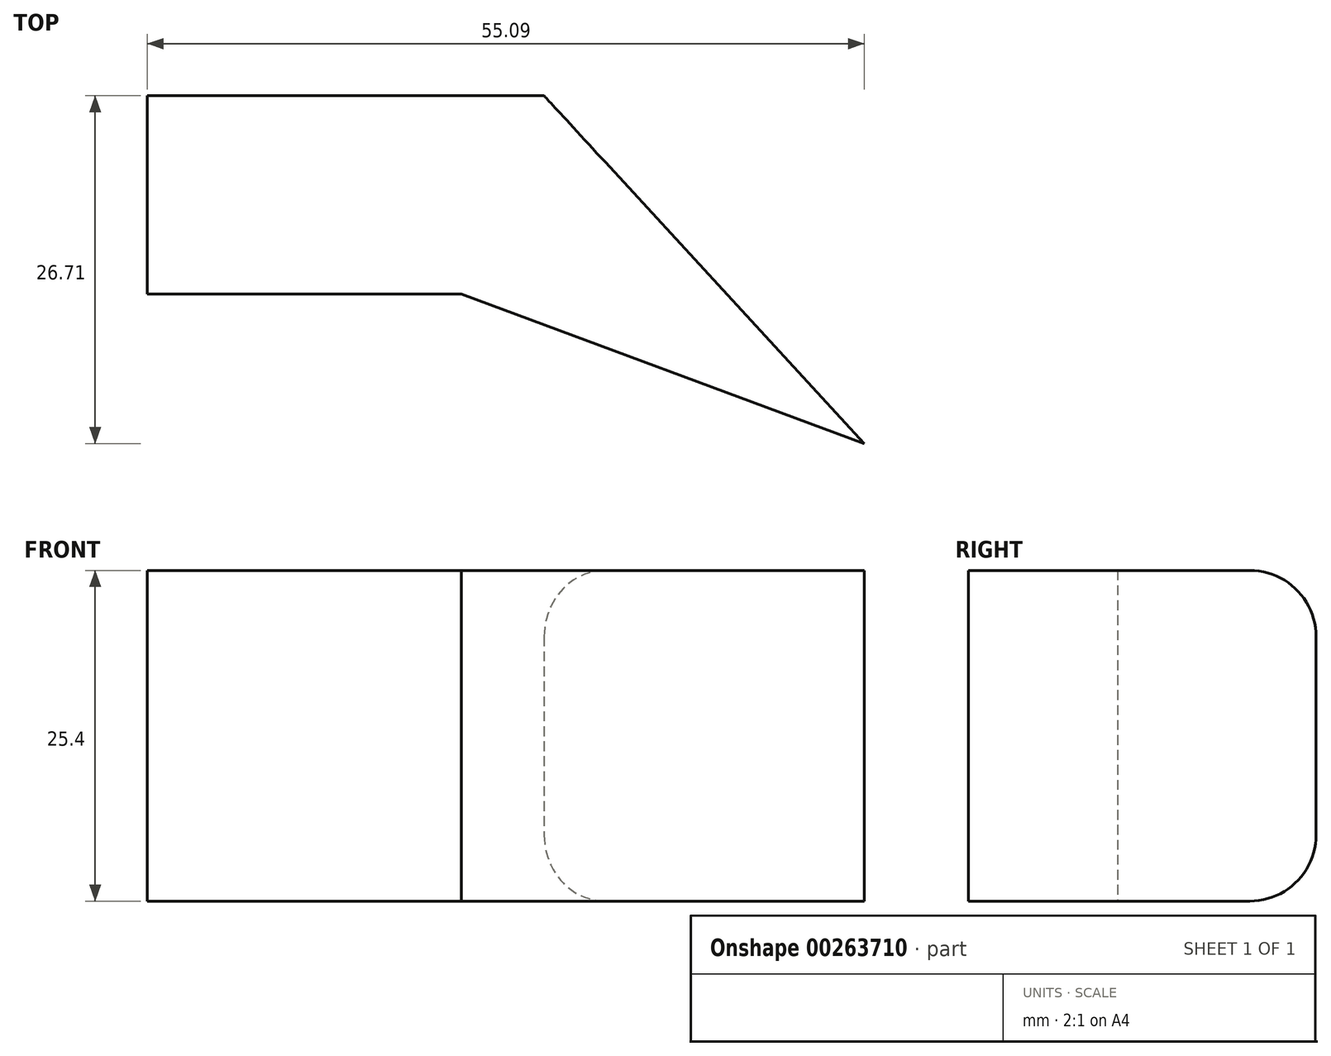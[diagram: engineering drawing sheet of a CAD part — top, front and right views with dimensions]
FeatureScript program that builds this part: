
annotation { "Feature Type Name" : "Feature", "Feature Type Description" : "" }
export const myFeature = defineFeature(function(context is Context, id is Id, definition is map)
    precondition{}
    {
        {
            var Q0;
            Q0=qCreatedBy(makeId("Top.planeOp"),FACE);
            var sketch = newSketch(context, id + "F0", { "sketchPlane" : qUnion([Q0])});
            skLineSegment(sketch, "E0", {"start": v(0, 0) * mm, "end": v(24.13, 0) * mm});
            skLineSegment(sketch, "E1", {"start": v(30.48, 15.24) * mm, "end": v(0, 15.24) * mm});
            skLineSegment(sketch, "E2", {"start": v(0, 15.24) * mm, "end": v(0, 0) * mm});
            skPoint(sketch, "E3.end.orphan", {"position": v(52.02, -1.7) * mm});
            skPoint(sketch, "E4.start.orphan", {"position": v(52.02, 7.58) * mm});
            skLineSegment(sketch, "E5", {"start": v(24.13, 0) * mm, "end": v(55.1, -11.47) * mm});
            skLineSegment(sketch, "E6", {"start": v(55.1, -11.47) * mm, "end": v(30.48, 15.24) * mm});
            skSolve(sketch);
        }
        {
            var Q0;
            Q0=makeQuery(id+"F0.imprint","IMPRINT",FACE,{"disambiguationData":[TD([[makeQuery(id+"F0.imprint","IMPRINT",EDGE,{"derivedFrom":sQuery(id+"F0.wireOp",EDGE,"E0")}),1.0]])]});
            extrude(context, id + "F1", {"entities" : qUnion([Q0]), "depth" : 25.4 * mm});
        }
        {
            var Q0;
            Q0=makeQuery(id+"F1.opExtrude","CAP_EDGE",EDGE,{"disambiguationData":[OSD([sQuery(id+"F0.wireOp",EDGE,"Z0H0DoV6-WUdK-9oxL-9MZb-PCZNIYnMg9Jc")])],"isStart":false});
            var Q1;
            Q1=makeQuery(id+"F1.opExtrude","SWEPT_EDGE",EDGE,{"disambiguationData":[OSD([sQuery(id+"F0.wireOp",EDGE,"RmBZrsqu-M6o7-0Kwk-3TkN-V8xLabiM8X2J"),sQuery(id+"F0.wireOp",EDGE,"Z0H0DoV6-WUdK-9oxL-9MZb-PCZNIYnMg9Jc")])]});
            var Q2;
            Q2=makeQuery(id+"F1.opExtrude","CAP_EDGE",EDGE,{"disambiguationData":[OSD([sQuery(id+"F0.wireOp",EDGE,"E4")])],"isStart":false});
            var Q3;
            Q3=makeQuery(id+"F1.opExtrude","CAP_EDGE",EDGE,{"disambiguationData":[OSD([sQuery(id+"F0.wireOp",EDGE,"E1")])],"isStart":false});
            fillet(context, id + "F2", {"entities" : qUnion([Q0, Q1, Q2, Q3]), "radius" : 5.08 * mm, "tangentPropagation" : true, "allowEdgeOverflow" : false});
        }
        {
            var Q0;
            Q0=makeQuery(id+"F1.opExtrude","CAP_EDGE",EDGE,{"disambiguationData":[OSD([sQuery(id+"F0.wireOp",EDGE,"E1")])],"isStart":true});
            var Q1;
            Q1=makeQuery(id+"F1.opExtrude","CAP_EDGE",EDGE,{"disambiguationData":[OSD([sQuery(id+"F0.wireOp",EDGE,"Z0H0DoV6-WUdK-9oxL-9MZb-PCZNIYnMg9Jc")])],"isStart":true});
            fillet(context, id + "F3", {"entities" : qUnion([Q0, Q1]), "radius" : 5.08 * mm, "tangentPropagation" : true, "allowEdgeOverflow" : false});
        }
    });
